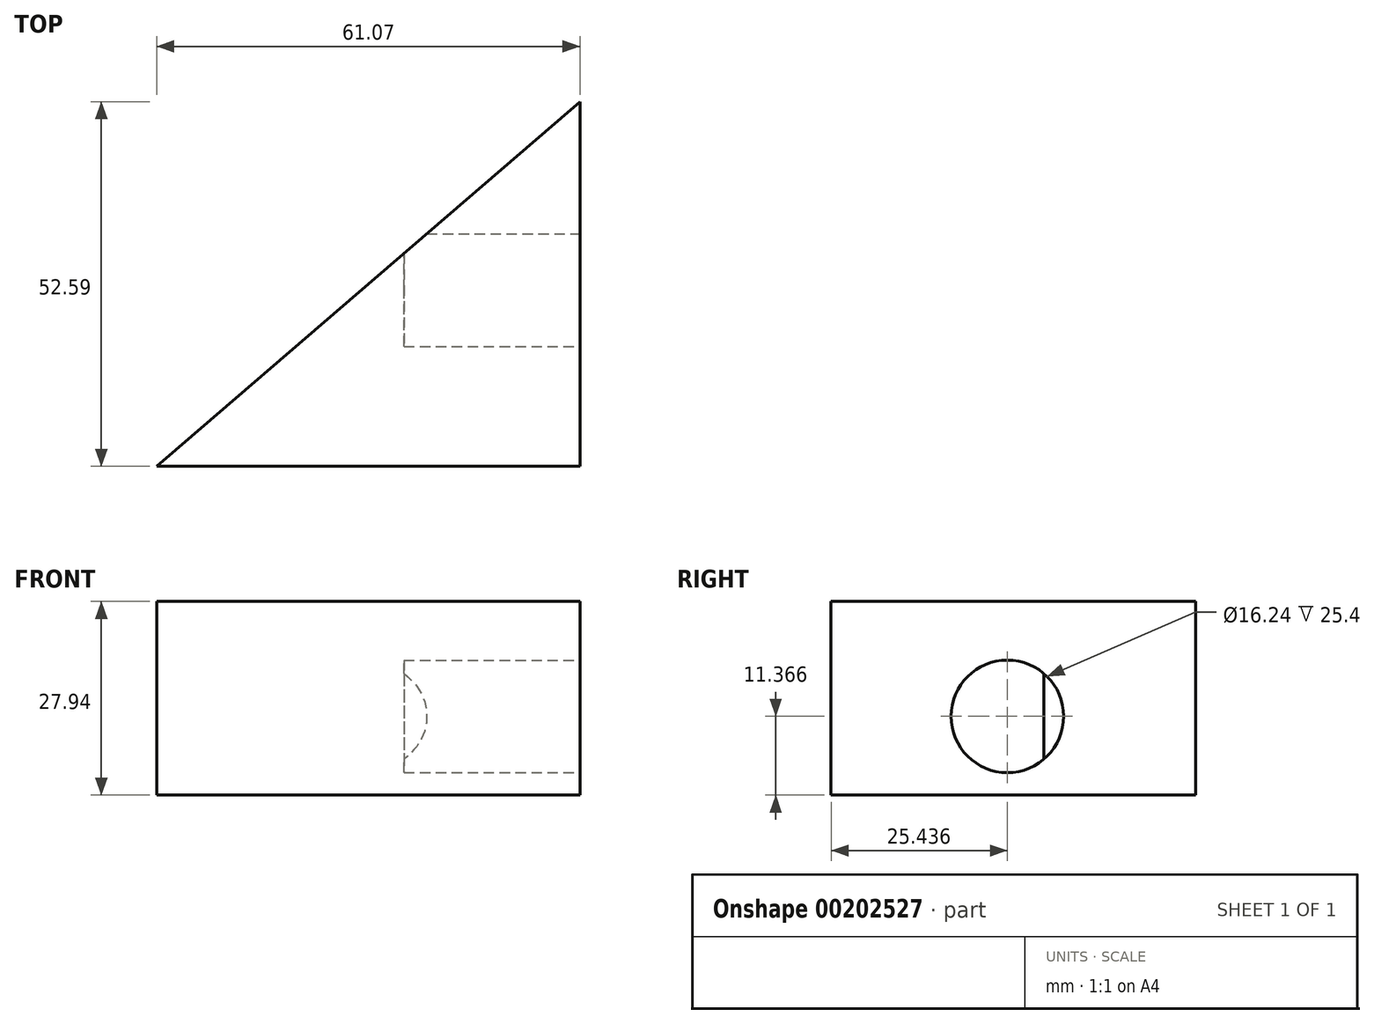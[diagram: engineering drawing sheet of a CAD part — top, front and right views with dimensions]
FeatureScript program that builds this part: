
annotation { "Feature Type Name" : "Feature", "Feature Type Description" : "" }
export const myFeature = defineFeature(function(context is Context, id is Id, definition is map)
    precondition{}
    {
        {
            var Q0;
            Q0=qCreatedBy(makeId("Top.planeOp"),FACE);
            var sketch = newSketch(context, id + "F0", { "sketchPlane" : qUnion([Q0])});
            skLineSegment(sketch, "E0", {"start": v(-46.18, -34.02) * mm, "end": v(14.89, -34.02) * mm});
            skLineSegment(sketch, "E1", {"start": v(14.89, -34.02) * mm, "end": v(14.89, 18.57) * mm});
            skLineSegment(sketch, "E2", {"start": v(14.89, 18.57) * mm, "end": v(-46.18, -34.02) * mm});
            skSolve(sketch);
        }
        {
            var Q0;
            Q0 = qSketchRegion(id + "F0", true);
            extrude(context, id + "F1", {"entities" : qUnion([Q0]), "oppositeDirection" : true, "depth" : 27.94 * mm});
        }
        {
            var Q0;
            Q0=makeQuery(id+"F1.opExtrude","SWEPT_FACE",FACE,{"disambiguationData":[OSD([sQuery(id+"F0.wireOp",EDGE,"E1")])]});
            var sketch = newSketch(context, id + "F2", { "sketchPlane" : qUnion([Q0])});
            skCircle(sketch, "E3", {"center": v(-8.58, -16.57) * mm, "radius": 8.12 * mm});
            skSolve(sketch);
        }
        {
            var Q0;
            Q0 = qSketchRegion(id + "F2", true);
            extrude(context, id + "F3", {"entities" : qUnion([Q0]), "operationType" : NewBodyOperationType.REMOVE, "oppositeDirection" : true, "depth" : 25.4 * mm});
        }
    });
